# Revit family: Faucet-Single-American_Standard-Berg-2009101_Series
name_source: partatom
category: Plumbing Fixtures
units: mm (PartAtom-declared; Revit-internal decimal feet)

## family parameters
Always vertical = No
Cut with Voids When Loaded = No
OmniClass Number = 23.45.55.14
OmniClass Title = Single Faucets
Part Type = Normal
Room Calculation Point = No
Round Connector Dimension = Use Diameter
Shared = Yes
Work Plane-Based = Yes

## types (1)
- 2009101.002
    2064.101P Escutcheon Plate = No
    ADA Compliant = Yes
    Assembly Code = D2020300
    CW Connection = Yes
    CWFU = 1.5
    Cold Water Connection Diameter = 3/8"
    Default Elevation = 0"
    Description = Berg Single Control Bathroom Sink Faucet. Lever handle. Metal pop-up drain. Polish Chrome finish.
    Finish = Brass-American Standard-002-Polished Chrome
    Flow Rate = 1 GPM
    HW Connection = Yes
    HWFU = 1.5
    Height = 5 1/2"
    Hot Water Connection Diameter = 3/8"
    Installation Type = Deck Mounted
    Length = 6 11/16"
    Manufacturer = American Standard
    Material = Brass-American Standard-002-Polished Chrome
    Model = 2009101.002
    Price = Prices may vary. Please consult Manufacturer Representative for most up-to-date price list.
    Product Documentation Link = https://www.americanstandard.ca
    Product Page URL = https://www.americanstandard.ca
    Revised Date = 04/23/2021
    Specification = Single control bathroom sink faucet shall feature a brass body and metal lever handle. Faucet shall be equipped with flexible supplies with 3/8in compression connectors. Shall also feature washerless ceramic disc valve cartridge. Faucet shall be American Standard Model 2009101.002.
    Type Comments = Available Accessory: 2064101P Escutcheon Plate Only.
    URL = http://www.americanstandard-us.com
    Vent Connection = No
    WFU = 2
    Warranty Information = Limited Lifetime Function and Finish Warranty
    Waste Connection = Yes
    Width = 1 13/16"

## geometry (parser evidence)
native form markers: Sweep x2
no freeform markers — native parametric forms only
